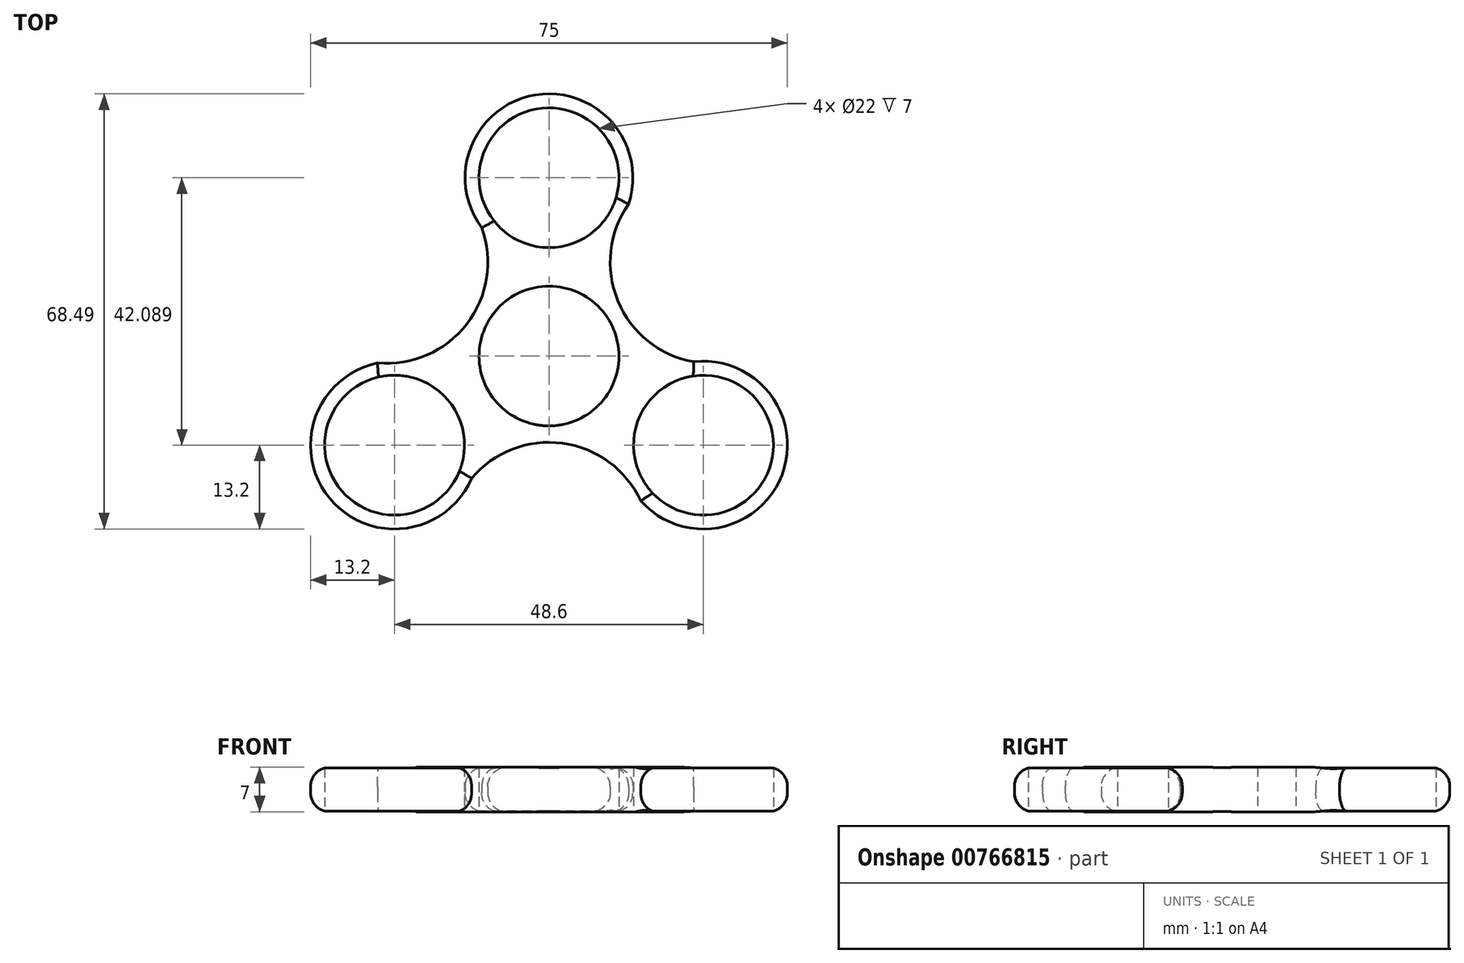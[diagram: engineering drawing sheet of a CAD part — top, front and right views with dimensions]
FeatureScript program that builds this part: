
annotation { "Feature Type Name" : "Feature", "Feature Type Description" : "" }
export const myFeature = defineFeature(function(context is Context, id is Id, definition is map)
    precondition{}
    {
        {
            var Q0;
            Q0=qCreatedBy(makeId("Top.planeOp"),FACE);
            var sketch = newSketch(context, id + "F0", { "sketchPlane" : qUnion([Q0])});
            skCircle(sketch, "E0", {"center": v(0, 0) * mm, "radius": 11 * mm});
            skCircle(sketch, "E1", {"center": v(0, 28.06) * mm, "radius": 11 * mm});
            skArc(sketch, "E2", {"start": v(10.58, 20.17) * mm, "mid": v(0, 41.26) * mm, "end": v(-10.58, 20.17) * mm});
            skArc(sketch, "E3.1.0", {"start": v(-22.76, -0.92) * mm, "mid": v(-35.73, -20.63) * mm, "end": v(-12.18, -19.25) * mm});
            skCircle(sketch, "E3.1.1", {"center": v(-24.3, -14.03) * mm, "radius": 11 * mm});
            skArc(sketch, "E3.2.0", {"start": v(12.18, -19.25) * mm, "mid": v(35.73, -20.63) * mm, "end": v(22.76, -0.92) * mm});
            skCircle(sketch, "E3.2.1", {"center": v(24.3, -14.03) * mm, "radius": 11 * mm});
            skArc(sketch, "E4", {"start": v(12.53, 23.91) * mm, "mid": v(10.83, 8.7) * mm, "end": v(22.76, -0.92) * mm});
            skArc(sketch, "E5.1.0", {"start": v(-26.97, -1.1) * mm, "mid": v(-12.94, 5.03) * mm, "end": v(-10.58, 20.17) * mm});
            skArc(sketch, "E5.2.0", {"start": v(14.44, -22.8) * mm, "mid": v(2.11, -13.73) * mm, "end": v(-12.18, -19.25) * mm});
            skSolve(sketch);
        }
        {
            var Q0;
            Q0=makeQuery(id+"F0.imprint","IMPRINT",FACE,{"disambiguationData":[TD([[makeQuery(id+"F0.imprint","IMPRINT",EDGE,{"derivedFrom":sQuery(id+"F0.wireOp",EDGE,"E0")}),-1.0]])]});
            extrude(context, id + "F1", {"entities" : qUnion([Q0]), "endBound" : BoundingType.SYMMETRIC, "depth" : 7 * mm, "offsetDistance" : 25 * mm});
        }
        {
            var Q0;
            Q0=makeQuery(id+"F1.opExtrude","CAP_EDGE",EDGE,{"disambiguationData":[OSD([sQuery(id+"F0.wireOp",EDGE,"E3.1.0")])],"isStart":true});
            var Q1;
            Q1=makeQuery(id+"F1.opExtrude","CAP_EDGE",EDGE,{"disambiguationData":[OSD([sQuery(id+"F0.wireOp",EDGE,"E5.1.0")])],"isStart":true});
            var Q2;
            Q2=makeQuery(id+"F1.opExtrude","CAP_EDGE",EDGE,{"disambiguationData":[OSD([sQuery(id+"F0.wireOp",EDGE,"E5.2.0")])],"isStart":true});
            var Q3;
            Q3=makeQuery(id+"F1.opExtrude","CAP_EDGE",EDGE,{"disambiguationData":[OSD([sQuery(id+"F0.wireOp",EDGE,"E3.2.0")])],"isStart":true});
            var Q4;
            Q4=makeQuery(id+"F1.opExtrude","CAP_EDGE",EDGE,{"disambiguationData":[OSD([sQuery(id+"F0.wireOp",EDGE,"E4")])],"isStart":true});
            var Q5;
            Q5=makeQuery(id+"F1.opExtrude","CAP_EDGE",EDGE,{"disambiguationData":[OSD([sQuery(id+"F0.wireOp",EDGE,"E2")])],"isStart":true});
            fillet(context, id + "F2", {"entities" : qUnion([Q0, Q1, Q2, Q3, Q4, Q5]), "radius" : 3 * mm, "tangentPropagation" : true, "allowEdgeOverflow" : false});
        }
        {
            var Q0;
            Q0=makeQuery(id+"F1.opExtrude","CAP_EDGE",EDGE,{"disambiguationData":[OSD([sQuery(id+"F0.wireOp",EDGE,"E2")])],"isStart":false});
            var Q1;
            Q1=makeQuery(id+"F1.opExtrude","CAP_EDGE",EDGE,{"disambiguationData":[OSD([sQuery(id+"F0.wireOp",EDGE,"E4")])],"isStart":false});
            var Q2;
            Q2=makeQuery(id+"F1.opExtrude","CAP_EDGE",EDGE,{"disambiguationData":[OSD([sQuery(id+"F0.wireOp",EDGE,"E3.2.0")])],"isStart":false});
            var Q3;
            Q3=makeQuery(id+"F1.opExtrude","CAP_EDGE",EDGE,{"disambiguationData":[OSD([sQuery(id+"F0.wireOp",EDGE,"E5.1.0")])],"isStart":false});
            var Q4;
            Q4=makeQuery(id+"F1.opExtrude","CAP_EDGE",EDGE,{"disambiguationData":[OSD([sQuery(id+"F0.wireOp",EDGE,"E3.1.0")])],"isStart":false});
            var Q5;
            Q5=makeQuery(id+"F1.opExtrude","CAP_EDGE",EDGE,{"disambiguationData":[OSD([sQuery(id+"F0.wireOp",EDGE,"E5.2.0")])],"isStart":false});
            fillet(context, id + "F3", {"entities" : qUnion([Q0, Q1, Q2, Q3, Q4, Q5]), "radius" : 3 * mm, "tangentPropagation" : true, "allowEdgeOverflow" : false});
        }
    });
